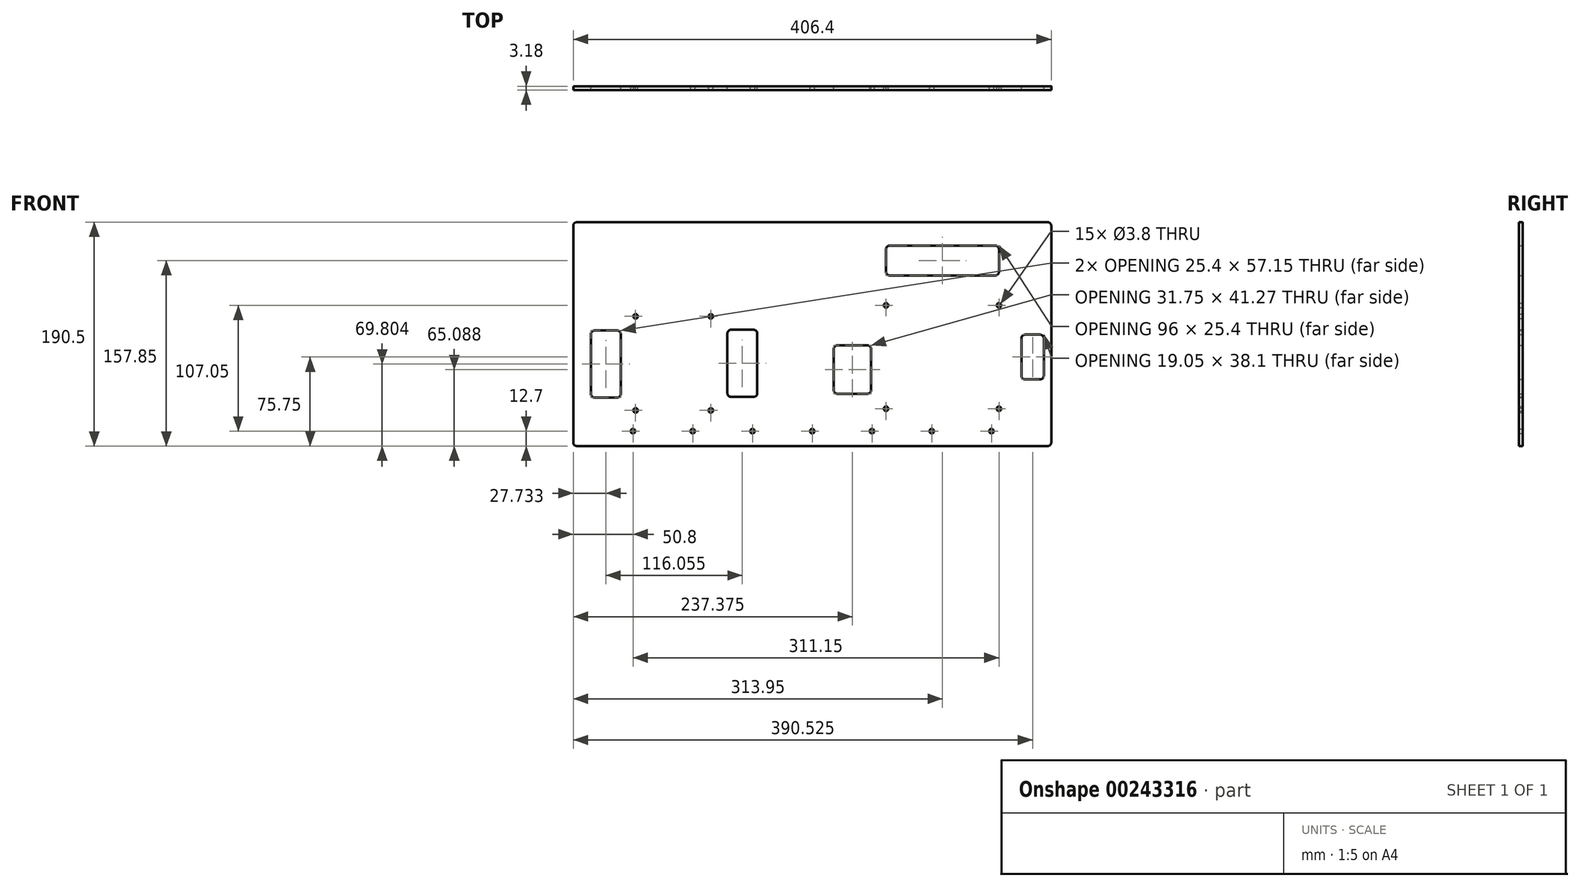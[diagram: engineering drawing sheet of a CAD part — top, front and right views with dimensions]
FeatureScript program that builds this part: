
annotation { "Feature Type Name" : "Feature", "Feature Type Description" : "" }
export const myFeature = defineFeature(function(context is Context, id is Id, definition is map)
    precondition{}
    {
        {
            var Q0;
            Q0=qCreatedBy(makeId("Front.planeOp"),FACE);
            var sketch = newSketch(context, id + "F0", { "sketchPlane" : qUnion([Q0])});
            skLineSegment(sketch, "E0.bottom", {"start": v(-200.03, 95.25) * mm, "end": v(200.03, 95.25) * mm});
            skLineSegment(sketch, "E0.top", {"start": v(-200.03, -95.25) * mm, "end": v(200.03, -95.25) * mm});
            skLineSegment(sketch, "E0.left", {"start": v(-203.2, 92.08) * mm, "end": v(-203.2, -92.08) * mm});
            skLineSegment(sketch, "E0.right", {"start": v(203.2, 92.08) * mm, "end": v(203.2, -92.07) * mm});
            skPoint(sketch, "E0.middle", {"position": v(0, 0) * mm});
            skLineSegment(sketch, "E1", {"start": v(-203.2, -82.55) * mm, "end": v(-152.4, -82.55) * mm, "construction": true});
            skCircle(sketch, "E2", {"center": v(-152.4, -82.55) * mm, "radius": 1.9 * mm});
            skCircle(sketch, "E3.1.0.0", {"center": v(-101.6, -82.55) * mm, "radius": 1.9 * mm});
            skCircle(sketch, "E3.2.0.0", {"center": v(-50.8, -82.55) * mm, "radius": 1.9 * mm});
            skCircle(sketch, "E3.3.0.0", {"center": v(0, -82.55) * mm, "radius": 1.9 * mm});
            skCircle(sketch, "E3.4.0.0", {"center": v(50.8, -82.55) * mm, "radius": 1.9 * mm});
            skCircle(sketch, "E3.5.0.0", {"center": v(101.6, -82.55) * mm, "radius": 1.9 * mm});
            skCircle(sketch, "E3.6.0.0", {"center": v(152.4, -82.55) * mm, "radius": 1.9 * mm});
            skLineSegment(sketch, "E3.direction1", {"start": v(-152.4, -82.55) * mm, "end": v(-101.6, -82.55) * mm, "construction": true});
            skCircle(sketch, "E4", {"center": v(158.75, -63.5) * mm, "radius": 1.9 * mm});
            skCircle(sketch, "E5.MirrorC", {"center": v(158.75, 24.5) * mm, "radius": 1.9 * mm});
            skCircle(sketch, "E6.3.0.1", {"center": v(62.75, 24.5) * mm, "radius": 1.9 * mm});
            skCircle(sketch, "E6.3.0.2", {"center": v(62.75, -63.5) * mm, "radius": 1.9 * mm});
            skLineSegment(sketch, "E7.bottom", {"start": v(62.75, 24.5) * mm, "end": v(158.75, 24.5) * mm, "construction": true});
            skLineSegment(sketch, "E7.top", {"start": v(62.75, -63.5) * mm, "end": v(158.75, -63.5) * mm, "construction": true});
            skLineSegment(sketch, "E7.left", {"start": v(62.75, 24.5) * mm, "end": v(62.75, -63.5) * mm, "construction": true});
            skLineSegment(sketch, "E7.right", {"start": v(158.75, 24.5) * mm, "end": v(158.75, -63.5) * mm, "construction": true});
            skLineSegment(sketch, "E8.bottom", {"start": v(-199.88, 94.93) * mm, "end": v(54.12, 94.93) * mm, "construction": true});
            skLineSegment(sketch, "E8.top", {"start": v(-199.88, 18.73) * mm, "end": v(54.12, 18.73) * mm, "construction": true});
            skLineSegment(sketch, "E8.left", {"start": v(-199.88, 94.93) * mm, "end": v(-199.88, 18.73) * mm, "construction": true});
            skLineSegment(sketch, "E8.right", {"start": v(54.12, 94.93) * mm, "end": v(54.12, 18.73) * mm, "construction": true});
            skPoint(sketch, "E8.middle", {"position": v(-72.88, 56.83) * mm});
            skLineSegment(sketch, "E9.bottom", {"start": v(65.93, 49.9) * mm, "end": v(155.58, 49.9) * mm});
            skLineSegment(sketch, "E9.top", {"start": v(65.93, 75.3) * mm, "end": v(155.58, 75.3) * mm});
            skLineSegment(sketch, "E9.left", {"start": v(62.75, 53.08) * mm, "end": v(62.75, 72.13) * mm});
            skLineSegment(sketch, "E9.right", {"start": v(158.75, 53.08) * mm, "end": v(158.75, 72.13) * mm});
            skPoint(sketch, "E9.middle", {"position": v(110.75, 62.6) * mm});
            skPoint(sketch, "E9.middle.positionSnap0", {"position": v(110.75, 24.5) * mm});
            skPoint(sketch, "E9.centerSnap0", {"position": v(110.75, 24.5) * mm});
            skLineSegment(sketch, "E10.bottom", {"start": v(21.48, -9.52) * mm, "end": v(46.88, -9.52) * mm});
            skLineSegment(sketch, "E10.top", {"start": v(21.48, -50.8) * mm, "end": v(46.88, -50.8) * mm});
            skLineSegment(sketch, "E10.left", {"start": v(18.3, -12.7) * mm, "end": v(18.3, -47.62) * mm});
            skLineSegment(sketch, "E10.right", {"start": v(50.05, -12.7) * mm, "end": v(50.05, -47.62) * mm});
            skPoint(sketch, "E10.middle", {"position": v(34.18, -30.16) * mm});
            skPoint(sketch, "E11.visualSharp", {"position": v(62.75, 75.3) * mm});
            skArc(sketch, "E11.filletArc", {"start": v(65.93, 75.3) * mm, "mid": v(63.68, 74.37) * mm, "end": v(62.75, 72.13) * mm});
            skPoint(sketch, "E12.visualSharp", {"position": v(62.75, 49.9) * mm});
            skArc(sketch, "E12.filletArc", {"start": v(62.75, 53.08) * mm, "mid": v(63.68, 50.83) * mm, "end": v(65.93, 49.9) * mm});
            skPoint(sketch, "E13.visualSharp", {"position": v(50.05, -9.52) * mm});
            skArc(sketch, "E13.filletArc", {"start": v(50.05, -12.7) * mm, "mid": v(49.12, -10.45) * mm, "end": v(46.88, -9.52) * mm});
            skPoint(sketch, "E14.visualSharp", {"position": v(18.3, -9.52) * mm});
            skArc(sketch, "E14.filletArc", {"start": v(21.48, -9.52) * mm, "mid": v(19.23, -10.45) * mm, "end": v(18.3, -12.7) * mm});
            skPoint(sketch, "E15.visualSharp", {"position": v(18.3, -50.8) * mm});
            skArc(sketch, "E15.filletArc", {"start": v(18.3, -47.62) * mm, "mid": v(19.23, -49.87) * mm, "end": v(21.48, -50.8) * mm});
            skPoint(sketch, "E16.visualSharp", {"position": v(50.05, -50.8) * mm});
            skArc(sketch, "E16.filletArc", {"start": v(46.88, -50.8) * mm, "mid": v(49.12, -49.87) * mm, "end": v(50.05, -47.62) * mm});
            skPoint(sketch, "E17.visualSharp", {"position": v(158.75, 49.9) * mm});
            skArc(sketch, "E17.filletArc", {"start": v(155.58, 49.9) * mm, "mid": v(157.82, 50.83) * mm, "end": v(158.75, 53.08) * mm});
            skPoint(sketch, "E18.visualSharp", {"position": v(158.75, 75.3) * mm});
            skArc(sketch, "E18.filletArc", {"start": v(158.75, 72.13) * mm, "mid": v(157.82, 74.37) * mm, "end": v(155.58, 75.3) * mm});
            skPoint(sketch, "E19.visualSharp", {"position": v(203.2, -95.25) * mm});
            skArc(sketch, "E19.filletArc", {"start": v(200.03, -95.25) * mm, "mid": v(202.27, -94.32) * mm, "end": v(203.2, -92.07) * mm});
            skPoint(sketch, "E20.visualSharp", {"position": v(203.2, 95.25) * mm});
            skArc(sketch, "E20.filletArc", {"start": v(203.2, 92.08) * mm, "mid": v(202.27, 94.32) * mm, "end": v(200.03, 95.25) * mm});
            skPoint(sketch, "E21.visualSharp", {"position": v(-203.2, 95.25) * mm});
            skArc(sketch, "E21.filletArc", {"start": v(-200.03, 95.25) * mm, "mid": v(-202.27, 94.32) * mm, "end": v(-203.2, 92.08) * mm});
            skPoint(sketch, "E22.visualSharp", {"position": v(-203.2, -95.25) * mm});
            skArc(sketch, "E22.filletArc", {"start": v(-203.2, -92.08) * mm, "mid": v(-202.27, -94.32) * mm, "end": v(-200.03, -95.25) * mm});
            skLineSegment(sketch, "E23.bottom", {"start": v(193.68, -38.55) * mm, "end": v(180.98, -38.55) * mm});
            skLineSegment(sketch, "E23.top", {"start": v(193.68, -0.45) * mm, "end": v(180.98, -0.45) * mm});
            skLineSegment(sketch, "E23.left", {"start": v(196.85, -35.37) * mm, "end": v(196.85, -3.62) * mm});
            skLineSegment(sketch, "E23.right", {"start": v(177.8, -35.37) * mm, "end": v(177.8, -3.62) * mm});
            skPoint(sketch, "E23.middle", {"position": v(187.33, -19.5) * mm});
            skPoint(sketch, "E23.middle.positionSnap0", {"position": v(158.75, -19.5) * mm});
            skPoint(sketch, "E23.centerSnap0", {"position": v(158.75, -19.5) * mm});
            skPoint(sketch, "E24.visualSharp", {"position": v(177.8, -0.45) * mm});
            skArc(sketch, "E24.filletArc", {"start": v(180.98, -0.45) * mm, "mid": v(178.73, -1.38) * mm, "end": v(177.8, -3.62) * mm});
            skPoint(sketch, "E25.visualSharp", {"position": v(196.85, -38.55) * mm});
            skArc(sketch, "E25.filletArc", {"start": v(193.68, -38.55) * mm, "mid": v(195.92, -37.62) * mm, "end": v(196.85, -35.37) * mm});
            skPoint(sketch, "E26.visualSharp", {"position": v(177.8, -38.55) * mm});
            skArc(sketch, "E26.filletArc", {"start": v(177.8, -35.37) * mm, "mid": v(178.73, -37.62) * mm, "end": v(180.98, -38.55) * mm});
            skPoint(sketch, "E27.visualSharp", {"position": v(196.85, -0.45) * mm});
            skArc(sketch, "E27.filletArc", {"start": v(196.85, -3.62) * mm, "mid": v(195.92, -1.38) * mm, "end": v(193.68, -0.45) * mm});
            skCircle(sketch, "E28.3.0.0", {"center": v(-150.21, 15.12) * mm, "radius": 1.9 * mm});
            skCircle(sketch, "E28.3.0.2", {"center": v(-150.21, -64.88) * mm, "radius": 1.9 * mm});
            skCircle(sketch, "E28.5.0.0", {"center": v(-86.21, 15.12) * mm, "radius": 1.9 * mm});
            skCircle(sketch, "E28.5.0.2", {"center": v(-86.21, -64.88) * mm, "radius": 1.9 * mm});
            skLineSegment(sketch, "E29.bottom", {"start": v(-150.21, 15.12) * mm, "end": v(-86.21, 15.12) * mm, "construction": true});
            skLineSegment(sketch, "E29.top", {"start": v(-150.21, -64.88) * mm, "end": v(-86.21, -64.88) * mm});
            skLineSegment(sketch, "E29.left", {"start": v(-150.21, 15.12) * mm, "end": v(-150.21, -64.88) * mm, "construction": true});
            skLineSegment(sketch, "E29.right", {"start": v(-86.21, 15.12) * mm, "end": v(-86.21, -64.88) * mm, "construction": true});
            skLineSegment(sketch, "E30.bottom", {"start": v(-68.94, 3.7) * mm, "end": v(-49.89, 3.7) * mm});
            skLineSegment(sketch, "E30.top", {"start": v(-68.94, -53.46) * mm, "end": v(-49.89, -53.46) * mm});
            skLineSegment(sketch, "E30.left", {"start": v(-72.11, 0.52) * mm, "end": v(-72.11, -50.28) * mm});
            skLineSegment(sketch, "E30.right", {"start": v(-46.71, 0.52) * mm, "end": v(-46.71, -50.28) * mm});
            skPoint(sketch, "E30.middle", {"position": v(-59.41, -24.88) * mm});
            skArc(sketch, "E31.filletArc", {"start": v(-46.71, 0.52) * mm, "mid": v(-47.64, 2.76) * mm, "end": v(-49.89, 3.7) * mm});
            skPoint(sketch, "E32.visualSharp", {"position": v(-72.11, 3.7) * mm});
            skArc(sketch, "E32.filletArc", {"start": v(-68.94, 3.7) * mm, "mid": v(-71.18, 2.76) * mm, "end": v(-72.11, 0.52) * mm});
            skArc(sketch, "E33.filletArc", {"start": v(-49.89, -53.46) * mm, "mid": v(-47.64, -52.53) * mm, "end": v(-46.71, -50.28) * mm});
            skPoint(sketch, "E34.visualSharp", {"position": v(-72.11, -53.46) * mm});
            skArc(sketch, "E34.filletArc", {"start": v(-72.11, -50.28) * mm, "mid": v(-71.18, -52.53) * mm, "end": v(-68.94, -53.46) * mm});
            skLineSegment(sketch, "E35.bottom", {"start": v(-185, 3.13) * mm, "end": v(-165.94, 3.13) * mm});
            skLineSegment(sketch, "E35.top", {"start": v(-185, -54.02) * mm, "end": v(-165.94, -54.02) * mm});
            skLineSegment(sketch, "E35.left", {"start": v(-188.17, -0.05) * mm, "end": v(-188.17, -50.85) * mm});
            skLineSegment(sketch, "E35.right", {"start": v(-162.77, -0.05) * mm, "end": v(-162.77, -50.85) * mm});
            skPoint(sketch, "E35.middle", {"position": v(-175.47, -25.45) * mm});
            skArc(sketch, "E36.filletArc", {"start": v(-162.77, -0.05) * mm, "mid": v(-163.7, 2.2) * mm, "end": v(-165.94, 3.13) * mm});
            skPoint(sketch, "E37.visualSharp", {"position": v(-188.17, 3.13) * mm});
            skArc(sketch, "E37.filletArc", {"start": v(-185, 3.13) * mm, "mid": v(-187.24, 2.2) * mm, "end": v(-188.17, -0.05) * mm});
            skArc(sketch, "E38.filletArc", {"start": v(-165.94, -54.02) * mm, "mid": v(-163.7, -53.1) * mm, "end": v(-162.77, -50.85) * mm});
            skPoint(sketch, "E39.visualSharp", {"position": v(-188.17, -54.02) * mm});
            skArc(sketch, "E39.filletArc", {"start": v(-188.17, -50.85) * mm, "mid": v(-187.24, -53.1) * mm, "end": v(-185, -54.02) * mm});
            skSolve(sketch);
        }
        {
            var Q0;
            Q0 = qSketchRegion(id + "F0", true);
            extrude(context, id + "F1", {"entities" : qUnion([Q0]), "depth" : 3.17 * mm});
        }
    });
